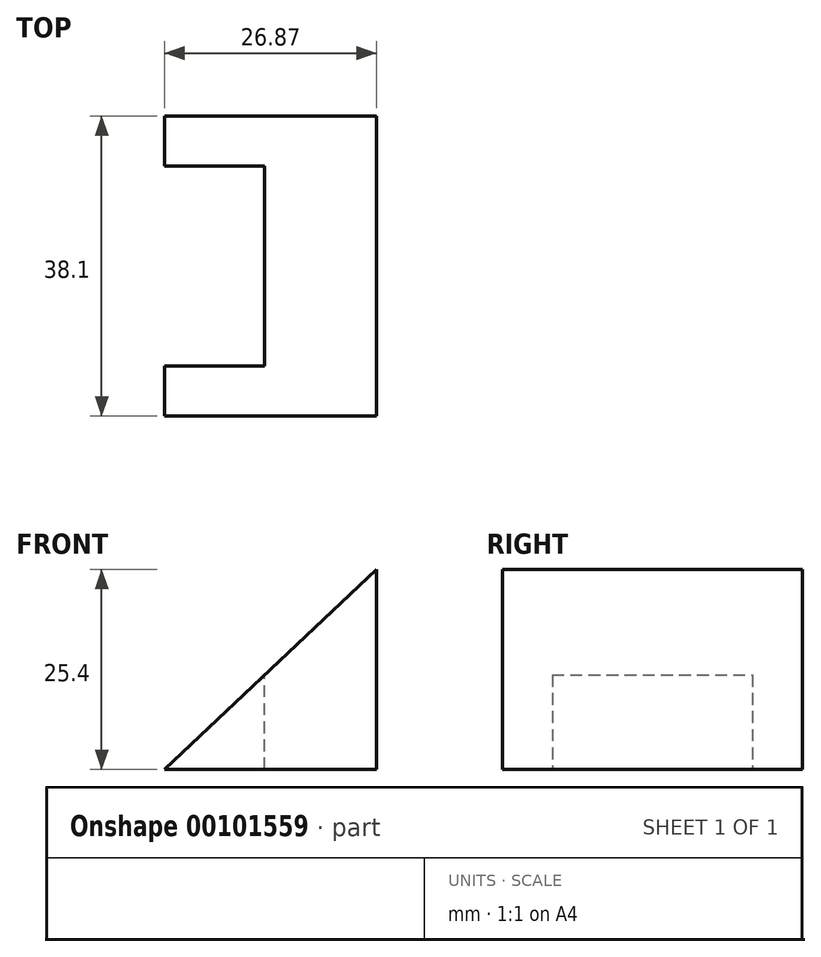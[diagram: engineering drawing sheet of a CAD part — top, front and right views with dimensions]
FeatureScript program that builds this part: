
annotation { "Feature Type Name" : "Feature", "Feature Type Description" : "" }
export const myFeature = defineFeature(function(context is Context, id is Id, definition is map)
    precondition{}
    {
        {
            var Q0;
            Q0=qCreatedBy(makeId("Front.planeOp"),FACE);
            var sketch = newSketch(context, id + "F0", { "sketchPlane" : qUnion([Q0])});
            skLineSegment(sketch, "E0", {"start": v(0, 0) * mm, "end": v(26.87, 0) * mm});
            skLineSegment(sketch, "E1", {"start": v(26.87, 0) * mm, "end": v(26.87, 25.4) * mm});
            skLineSegment(sketch, "E2", {"start": v(26.87, 25.4) * mm, "end": v(0, 0) * mm});
            skSolve(sketch);
        }
        {
            var Q0;
            Q0=makeQuery(id+"F0.imprint","IMPRINT",FACE,{"disambiguationData":[TD([[makeQuery(id+"F0.imprint","IMPRINT",EDGE,{"derivedFrom":sQuery(id+"F0.wireOp",EDGE,"E0")}),1.0]])]});
            extrude(context, id + "F1", {"entities" : qUnion([Q0]), "endBound" : BoundingType.SYMMETRIC, "depth" : 38.1 * mm});
        }
        {
            var Q0;
            Q0=qCreatedBy(makeId("Front.planeOp"),FACE);
            var sketch = newSketch(context, id + "F2", { "sketchPlane" : qUnion([Q0])});
            skLineSegment(sketch, "E3", {"start": v(0, 0) * mm, "end": v(12.7, 0) * mm});
            skLineSegment(sketch, "E4", {"start": v(12.7, 0) * mm, "end": v(12.7, 12.7) * mm});
            skLineSegment(sketch, "E5", {"start": v(12.7, 12.7) * mm, "end": v(0, 0) * mm});
            skSolve(sketch);
        }
        {
            var Q0;
            Q0 = qSketchRegion(id + "F2", true);
            extrude(context, id + "F3", {"entities" : qUnion([Q0]), "operationType" : NewBodyOperationType.REMOVE, "endBound" : BoundingType.SYMMETRIC, "depth" : 25.4 * mm});
        }
    });
